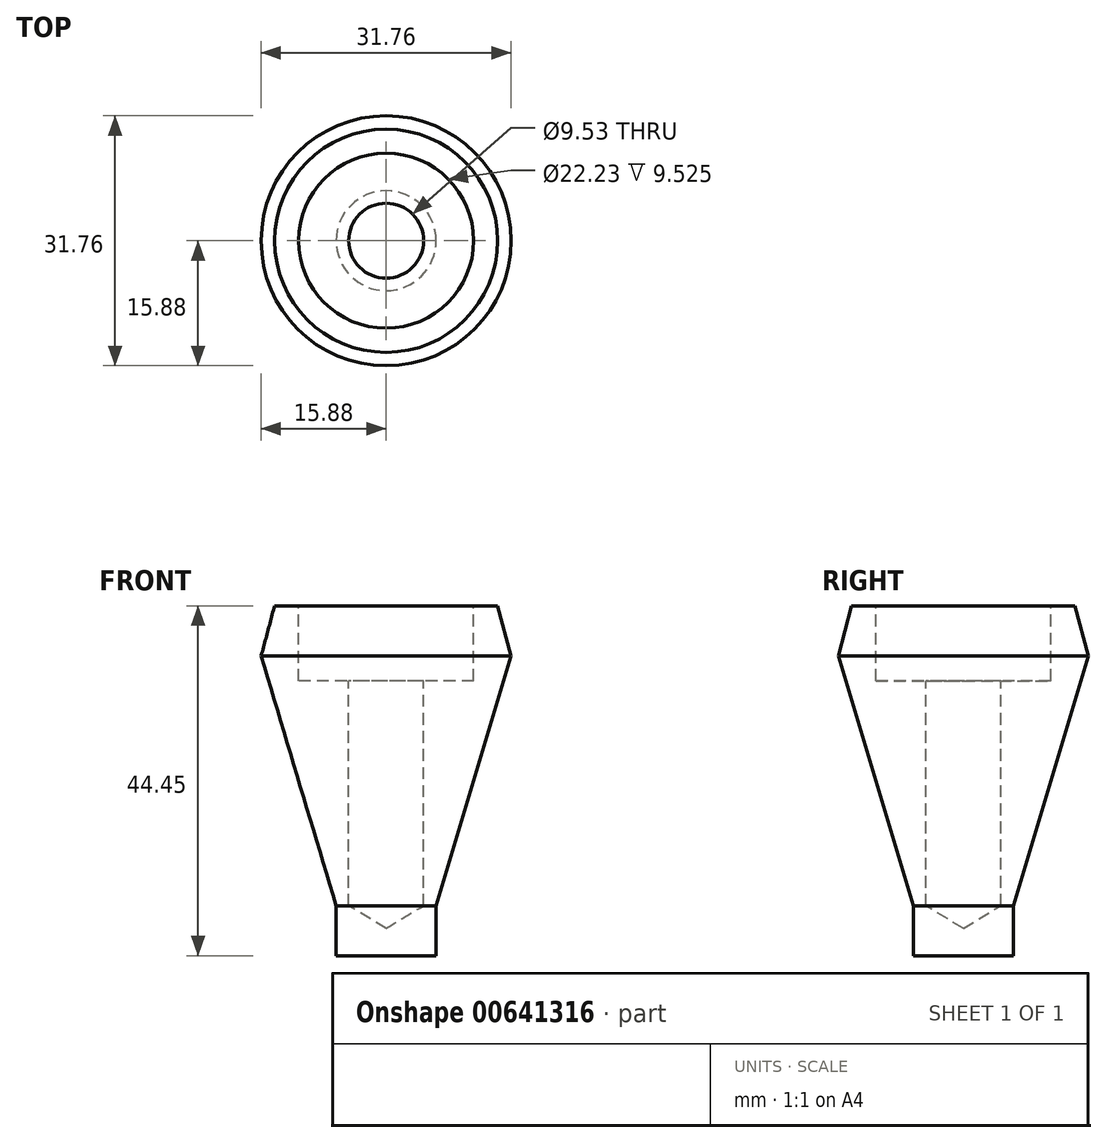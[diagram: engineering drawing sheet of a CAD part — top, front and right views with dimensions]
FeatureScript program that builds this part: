
annotation { "Feature Type Name" : "Feature", "Feature Type Description" : "" }
export const myFeature = defineFeature(function(context is Context, id is Id, definition is map)
    precondition{}
    {
        {
            var Q0;
            Q0=qCreatedBy(makeId("Front.planeOp"),FACE);
            var sketch = newSketch(context, id + "F0", { "sketchPlane" : qUnion([Q0])});
            skLineSegment(sketch, "E0", {"start": v(0, 0) * mm, "end": v(6.35, 0) * mm});
            skLineSegment(sketch, "E1", {"start": v(6.35, 0) * mm, "end": v(6.35, 6.35) * mm});
            skLineSegment(sketch, "E2", {"start": v(0, 0) * mm, "end": v(0, 38.1) * mm});
            skLineSegment(sketch, "E3", {"start": v(15.88, 38.1) * mm, "end": v(6.35, 6.35) * mm});
            skLineSegment(sketch, "E4", {"start": v(15.88, 38.1) * mm, "end": v(14.17, 44.45) * mm});
            skLineSegment(sketch, "E5", {"start": v(0, 0) * mm, "end": v(0, 44.45) * mm});
            skLineSegment(sketch, "E6", {"start": v(0, 44.45) * mm, "end": v(14.17, 44.45) * mm});
            skSolve(sketch);
        }
        {
            var Q0;
            {var subQ0=sQuery(id+"F0.wireOp",EDGE,"E0");Q0=makeQuery(id+"F0.imprint","IMPRINT",FACE,{"disambiguationData":[TD([[makeQuery(id+"F0.imprint","IMPRINT",EDGE,{"derivedFrom":subQ0}),1.0]])]});}
            var Q1;
            Q1=sQuery(id+"F0.wireOp",EDGE,"E5");
            revolve(context, id + "F1", {"entities" : qUnion([Q0]), "axis" : qUnion([Q1]), "revolveType" : RevolveType.FULL});
        }
        {
            var Q0;
            Q0=makeQuery(id+"F1.opRevolve","SWEPT_FACE",FACE,{"disambiguationData":[OSD([sQuery(id+"F0.wireOp",EDGE,"E6")])]});
            var sketch = newSketch(context, id + "F2", { "sketchPlane" : qUnion([Q0])});
            skPoint(sketch, "E7.0", {"position": v(0, 0) * mm});
            skSolve(sketch);
        }
        {
            var Q0;
            Q0=sQuery(id+"F2.wireOp",VERTEX,"E7.0");
            var Q1;
            Q1=makeQuery(id+"F1.opRevolve","SWEPT_BODY",BODY,{"disambiguationData":[OSD([sQuery(id+"F0.wireOp",EDGE,"E0"),sQuery(id+"F0.wireOp",EDGE,"E1"),sQuery(id+"F0.wireOp",EDGE,"E3"),sQuery(id+"F0.wireOp",EDGE,"E4"),sQuery(id+"F0.wireOp",EDGE,"E5"),sQuery(id+"F0.wireOp",EDGE,"E6")])]});
            hole(context, id + "F3", {"style" : HoleStyle.C_BORE, "endStyle" : HoleEndStyle.BLIND, "holeDiameter" : 9.52 * mm, "cBoreDiameter" : 22.22 * mm, "cBoreDepth" : 9.52 * mm, "majorDiameter" : 6.35 * mm, "holeDepth" : 38.1 * mm, "isTappedThrough" : true, "tappedDepth" : 12.7 * mm, "tapClearance" : 3, "locations" : qUnion([Q0]), "scope" : qUnion([Q1])});
        }
    });
